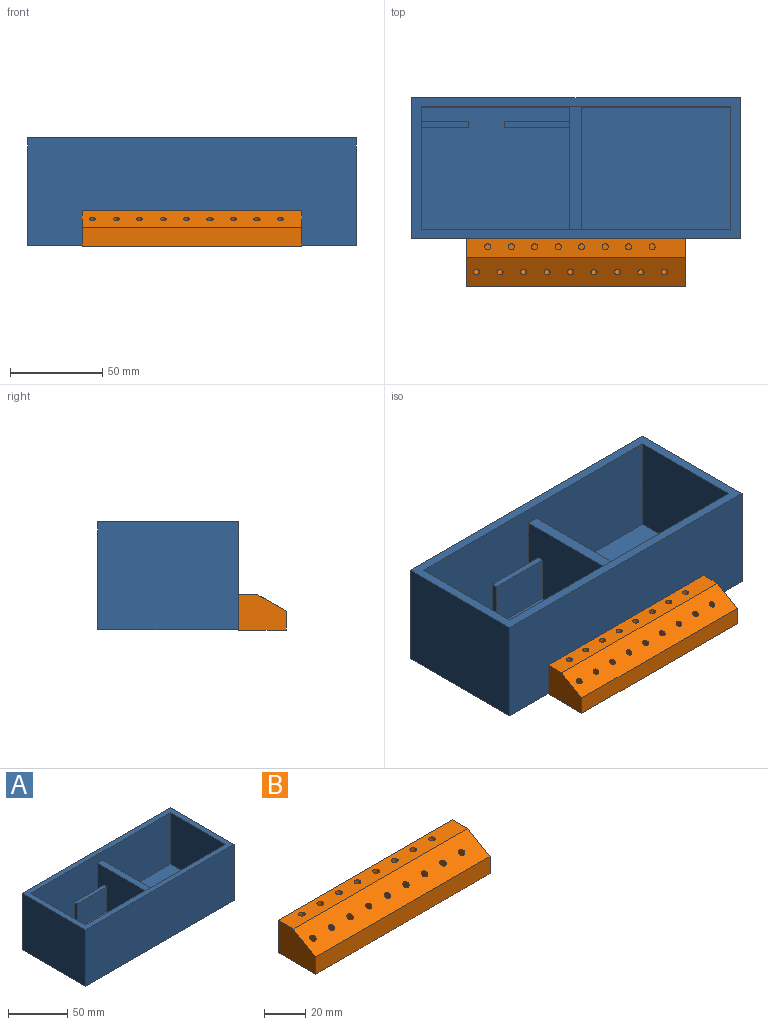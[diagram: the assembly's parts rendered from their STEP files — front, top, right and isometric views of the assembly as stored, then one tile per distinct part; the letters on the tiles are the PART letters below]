
ASSEMBLY  parts=2 mates=1
PART A: 23 faces, bbox 177.8x76.2x58.4 mm
  f0: plane 80.41x66.04mm, normal (0,0,1), area 5097.1mm2, adj f1,f2,f4,f12,f15,f16,f17,f19
  f1: plane 66.04x44.45mm, normal (-1,0,0), area 2847mm2, adj f0,f4,f12,f14,f19,f21,f22
  f2: plane 66.04x53.34mm, normal (1,0,0), area 3434.1mm2, adj f0,f4,f5,f12,f15,f16,f18
  f3: plane 80.88x66.04mm, normal (0,0,1), area 5341.1mm2, adj f4,f11,f12,f13
  f4: plane 167.64x53.34mm, normal (0,1,0), area 8659.7mm2, adj f0,f1,f2,f3,f5,f11,f13,f14
  f5: plane 177.8x76.2mm, normal (0,0,1), area 2477.4mm2, adj f2,f4,f6,f7,f8,f9,f11,f12
  f6: plane 177.8x58.42mm, normal (0,-1,0), area 10387.1mm2, adj f5,f7,f9,f10
  f7: plane 76.2x58.42mm, normal (1,0,0), area 4451.6mm2, adj f5,f6,f8,f10
  f8: plane 177.8x58.42mm, normal (0,1,0), area 10387.1mm2, adj f5,f7,f9,f10
  f9: plane 76.2x58.42mm, normal (-1,0,0), area 4451.6mm2, adj f5,f6,f8,f10
  f10: plane 177.8x76.2mm, normal (0,0,-1), area 13548.4mm2, adj f6,f7,f8,f9
  f11: plane 66.04x53.34mm, normal (-1,0,0), area 3522.6mm2, adj f3,f4,f5,f12
  f12: plane 167.64x53.34mm, normal (0,-1,0), area 8659.7mm2, adj f0,f1,f2,f3,f5,f11,f13,f14
  f13: plane 66.04x44.45mm, normal (1,0,0), area 2935.5mm2, adj f3,f4,f12,f14
  f14: plane 66.04x6.35mm, normal (0,0,1), area 419.4mm2, adj f1,f4,f12,f13
  f15: plane 25.83x25.4mm, normal (0,1,0), area 656.2mm2, adj f0,f2,f17,f18
  f16: plane 25.83x25.4mm, normal (0,-1,0), area 656.2mm2, adj f0,f2,f17,f18
  f17: plane 25.4x3.48mm, normal (1,0,0), area 88.5mm2, adj f0,f15,f16,f18
  f18: plane 25.83x3.48mm, normal (0,0,1), area 90mm2, adj f2,f15,f16,f17
  f19: plane 35.42x25.4mm, normal (0,1,0), area 899.6mm2, adj f0,f1,f20,f22
  f20: plane 25.4x3.48mm, normal (-1,0,0), area 88.5mm2, adj f0,f19,f21,f22
  f21: plane 35.42x25.4mm, normal (0,-1,0), area 899.6mm2, adj f0,f1,f20,f22
  f22: plane 35.42x3.48mm, normal (0,0,1), area 123.4mm2, adj f1,f19,f20,f21
PART B: 41 faces, bbox 119x25.9x19.1 mm
  f0: plane 118.96x10.16mm, normal (0,-1,0), area 1208.6mm2, adj f1,f3,f5,f6
  f1: plane 25.88x19.05mm, normal (1,0,0), area 424.6mm2, adj f0,f2,f4,f5,f6
  f2: plane 118.96x19.05mm, normal (0,1,0), area 2266.1mm2, adj f1,f3,f4,f5
  f3: plane 25.88x19.05mm, normal (-1,0,0), area 424.6mm2, adj f0,f2,f4,f5,f6
  f4: plane 118.96x10.48mm, normal (0,0,1), area 1178.6mm2, adj f1,f2,f3,f6,f25,f27,f29,f31
  f5: plane 118.96x25.88mm, normal (0,0,-1), area 3078.8mm2, adj f0,f1,f2,f3
  f6: plane 118.96x15.4mm, normal (0,-0.5,0.87), area 2038mm2, adj f0,f1,f3,f4,f7,f9,f11,f13
  f7: cylinder r=1.65mm len=12.65mm, axis (0,-0.5,0.87), area 131.7mm2, adj f6,f8
  f8: plane 3.3x2.86mm, normal (0,-0.5,0.87), area 8.6mm2, adj f7
  f9: cylinder r=1.65mm len=12.65mm, axis (0,-0.5,0.87), area 131.7mm2, adj f6,f10
  f10: plane 3.3x2.86mm, normal (0,-0.5,0.87), area 8.6mm2, adj f9
  f11: cylinder r=1.65mm len=12.65mm, axis (0,-0.5,0.87), area 131.7mm2, adj f6,f12
  f12: plane 3.3x2.86mm, normal (0,-0.5,0.87), area 8.6mm2, adj f11
  f13: cylinder r=1.65mm len=12.65mm, axis (0,-0.5,0.87), area 131.7mm2, adj f6,f14
  f14: plane 3.3x2.86mm, normal (0,-0.5,0.87), area 8.6mm2, adj f13
  f15: cylinder r=1.65mm len=12.65mm, axis (0,-0.5,0.87), area 131.7mm2, adj f6,f16
  f16: plane 3.3x2.86mm, normal (0,-0.5,0.87), area 8.6mm2, adj f15
  f17: cylinder r=1.65mm len=12.65mm, axis (0,-0.5,0.87), area 131.7mm2, adj f6,f18
  f18: plane 3.3x2.86mm, normal (0,-0.5,0.87), area 8.6mm2, adj f17
  f19: cylinder r=1.65mm len=12.65mm, axis (0,-0.5,0.87), area 131.7mm2, adj f6,f20
  f20: plane 3.3x2.86mm, normal (0,-0.5,0.87), area 8.6mm2, adj f19
  f21: cylinder r=1.65mm len=12.65mm, axis (0,-0.5,0.87), area 131.7mm2, adj f6,f22
  f22: plane 3.3x2.86mm, normal (0,-0.5,0.87), area 8.6mm2, adj f21
  f23: cylinder r=1.65mm len=12.65mm, axis (0,-0.5,0.87), area 131.7mm2, adj f6,f24
  f24: plane 3.3x2.86mm, normal (0,-0.5,0.87), area 8.6mm2, adj f23
  f25: cylinder r=1.65mm len=16.51mm, axis (0,0,1), area 171.3mm2, adj f4,f26
  f26: plane 3.3x3.3mm, normal (0,0,1), area 8.6mm2, adj f25
  f27: cylinder r=1.65mm len=16.51mm, axis (0,0,1), area 171.3mm2, adj f4,f28
  f28: plane 3.3x3.3mm, normal (0,0,1), area 8.6mm2, adj f27
  f29: cylinder r=1.65mm len=16.51mm, axis (0,0,1), area 171.3mm2, adj f4,f30
  f30: plane 3.3x3.3mm, normal (0,0,1), area 8.6mm2, adj f29
  f31: cylinder r=1.65mm len=16.51mm, axis (0,0,1), area 171.3mm2, adj f4,f32
  f32: plane 3.3x3.3mm, normal (0,0,1), area 8.6mm2, adj f31
  f33: cylinder r=1.65mm len=16.51mm, axis (0,0,1), area 171.3mm2, adj f4,f34
  f34: plane 3.3x3.3mm, normal (0,0,1), area 8.6mm2, adj f33
  f35: cylinder r=1.65mm len=16.51mm, axis (0,0,1), area 171.3mm2, adj f4,f36
  f36: plane 3.3x3.3mm, normal (0,0,1), area 8.6mm2, adj f35
  f37: cylinder r=1.65mm len=16.51mm, axis (0,0,1), area 171.3mm2, adj f4,f38
  f38: plane 3.3x3.3mm, normal (0,0,1), area 8.6mm2, adj f37
  f39: cylinder r=1.65mm len=16.51mm, axis (0,0,1), area 171.3mm2, adj f4,f40
  f40: plane 3.3x3.3mm, normal (0,0,1), area 8.6mm2, adj f39
PLACE A t=(3.11,-24.47,-39.4)mm
PLACE B t=(3.11,-75.51,-39.47)mm
MATE fastened B.f2 <-> A.f6  axis (0,1,0) through (3.11,-62.57,-29.95)mm
